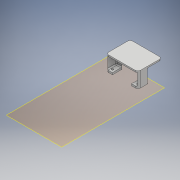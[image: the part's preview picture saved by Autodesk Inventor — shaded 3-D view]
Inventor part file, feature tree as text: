
AUTODESK INVENTOR PART (.ipt)
format: ipt  version: 2017 (Build 210142000, 142)  size: 285,184 bytes
history: native  units: mm
features: projected_geometry x6, extrude x4, sketch x4, fillet x3, other x2, plane x1, reference x1
ambient origin geometry x8: Origin, YZ Plane, XZ Plane, XY Plane, X Axis, Y Axis, Z Axis, Center Point
bodies: Solid1 (feature_tree)
feature tree (21):
  plane  "Work Plane1"
  extrude  "Extrusion1"  Depth=4.0mm
  extrude  "Extrusion2"  Depth=6.0mm
  extrude  "Extrusion3"  Depth=4.0mm
  fillet  "Fillet1"  Radius=4.0mm
  extrude  "Extrusion4"  Depth=5.5mm TaperAngle=0.0deg
  fillet  "Fillet2"  Radius=2.0mm
  fillet  "Fillet3"  Radius=50.0mm
  sketch  "Sketch1"  dims[d0=4.0mm d1=0.0mm d2=6.0mm]
  reference  "Reference1"
  sketch  "Sketch2"  dims[d3=6.0mm d4=6.0mm]
  projected_geometry  "Projected Loop1"
  projected_geometry  "Projected Loop2"
  sketch  "Sketch3"  dims[d5=6.0mm d6=4.0mm d7=4.0mm]
  projected_geometry  "Projected Loop3"
  projected_geometry  "Projected Loop4"
  sketch  "Sketch4"  dims[d8=7.0mm d9=0.0mm d10=25.0mm d11=0.0mm d12=2.0mm d13=50.0mm d14=3.0mm d15=0.0mm d16=2.0mm d17=5.5mm]
  projected_geometry  "Projected Loop5"
  projected_geometry  "Projected Loop6"
  other  "Assembly1"
  other  "ChassiUnico:1"
